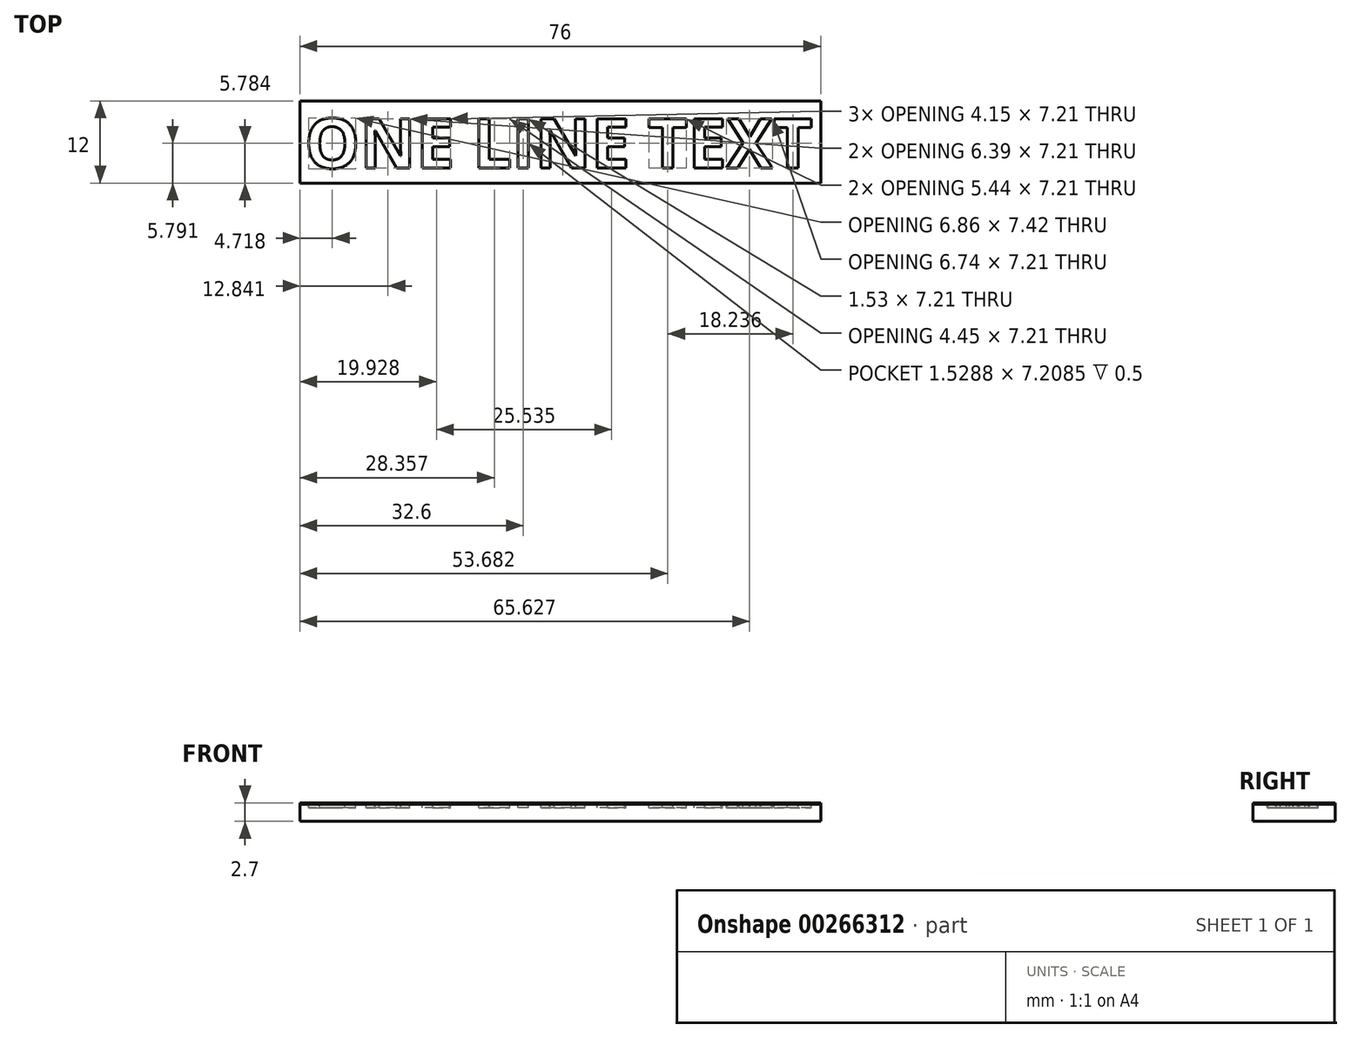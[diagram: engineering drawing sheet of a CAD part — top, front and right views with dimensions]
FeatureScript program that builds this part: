
annotation { "Feature Type Name" : "Feature", "Feature Type Description" : "" }
export const myFeature = defineFeature(function(context is Context, id is Id, definition is map)
    precondition{}
    {
        {
            var Q0;
            Q0=qCreatedBy(makeId("Top.planeOp"),FACE);
            var sketch = newSketch(context, id + "F0", { "sketchPlane" : qUnion([Q0])});
            skLineSegment(sketch, "E0.bottom", {"start": v(38, -6) * mm, "end": v(-38, -6) * mm});
            skLineSegment(sketch, "E0.top", {"start": v(38, 6) * mm, "end": v(-38, 6) * mm});
            skLineSegment(sketch, "E0.left", {"start": v(38, -6) * mm, "end": v(38, 6) * mm});
            skLineSegment(sketch, "E0.right", {"start": v(-38, -6) * mm, "end": v(-38, 6) * mm});
            skPoint(sketch, "E0.middle", {"position": v(0, 0) * mm});
            skSolve(sketch);
        }
        {
            var Q0;
            Q0=makeQuery(id+"F0.imprint","IMPRINT",FACE,{"disambiguationData":[TD([[makeQuery(id+"F0.imprint","IMPRINT",EDGE,{"derivedFrom":sQuery(id+"F0.wireOp",EDGE,"E0.bottom")}),-1.0]])]});
            extrude(context, id + "F1", {"entities" : qUnion([Q0]), "depth" : 2.5 * mm});
        }
        {
            var Q0;
            Q0=makeQuery(id+"F1.opExtrude","CAP_FACE",FACE,{"disambiguationData":[OSD([sQuery(id+"F0.wireOp",EDGE,"E0.bottom"),sQuery(id+"F0.wireOp",EDGE,"E0.top"),sQuery(id+"F0.wireOp",EDGE,"E0.left"),sQuery(id+"F0.wireOp",EDGE,"E0.right")])],"isStart":false});
            var sketch = newSketch(context, id + "F2", { "sketchPlane" : qUnion([Q0])});
            skText(sketch, "E1", { "text": "ONE LINE TEXT", "fontName": "OpenSans-Bold.ttf"});
            const initialGuessF2  = {"E1": [-0.0373, -0.00382, 1, 0, 0.00727]};
            skSetInitialGuess(sketch, initialGuessF2);
            skSolve(sketch);
        }
        {
            var Q0;
            Q0 = qSketchRegion(id + "F2", true);
            extrude(context, id + "F3", {"entities" : qUnion([Q0]), "operationType" : NewBodyOperationType.REMOVE, "oppositeDirection" : true, "depth" : 0.5 * mm});
        }
        {
            var Q0;
            {var subQ0=sQuery(id+"F0.wireOp",EDGE,"E0.bottom");var subQ1=sQuery(id+"F0.wireOp",EDGE,"E0.right");var subQ2=sQuery(id+"F0.wireOp",EDGE,"E0.left");var subQ3=sQuery(id+"F0.wireOp",EDGE,"E0.top");Q0=makeQuery(id+"F3.boolean.opBoolean","SPLIT",FACE,{"disambiguationData":[TD([makeQuery(id+"F1.opExtrude","SWEPT_FACE",FACE,{"disambiguationData":[OSD([subQ0])]})])],"derivedFrom":makeQuery(id+"F1.opExtrude","CAP_FACE",FACE,{"disambiguationData":[OSD([subQ0,subQ3,subQ2,subQ1])],"isStart":false})});}
            var Q1;
            Q1=makeQuery(id+"F3.boolean.opBoolean","SPLIT",FACE,{"disambiguationData":[TD([makeQuery(id+"F3.opExtrude","SWEPT_FACE",FACE,{"disambiguationData":[OSD([sQuery(id+"F2.wireOp",EDGE,"E1.sketch_text.stroke-8")])]})])],"derivedFrom":makeQuery(id+"F1.opExtrude","CAP_FACE",FACE,{"disambiguationData":[OSD([sQuery(id+"F0.wireOp",EDGE,"E0.bottom"),sQuery(id+"F0.wireOp",EDGE,"E0.top"),sQuery(id+"F0.wireOp",EDGE,"E0.left"),sQuery(id+"F0.wireOp",EDGE,"E0.right")])],"isStart":false})});
            extrude(context, id + "F4", {"entities" : qUnion([Q0, Q1]), "depth" : 0.2 * mm});
        }
    });
